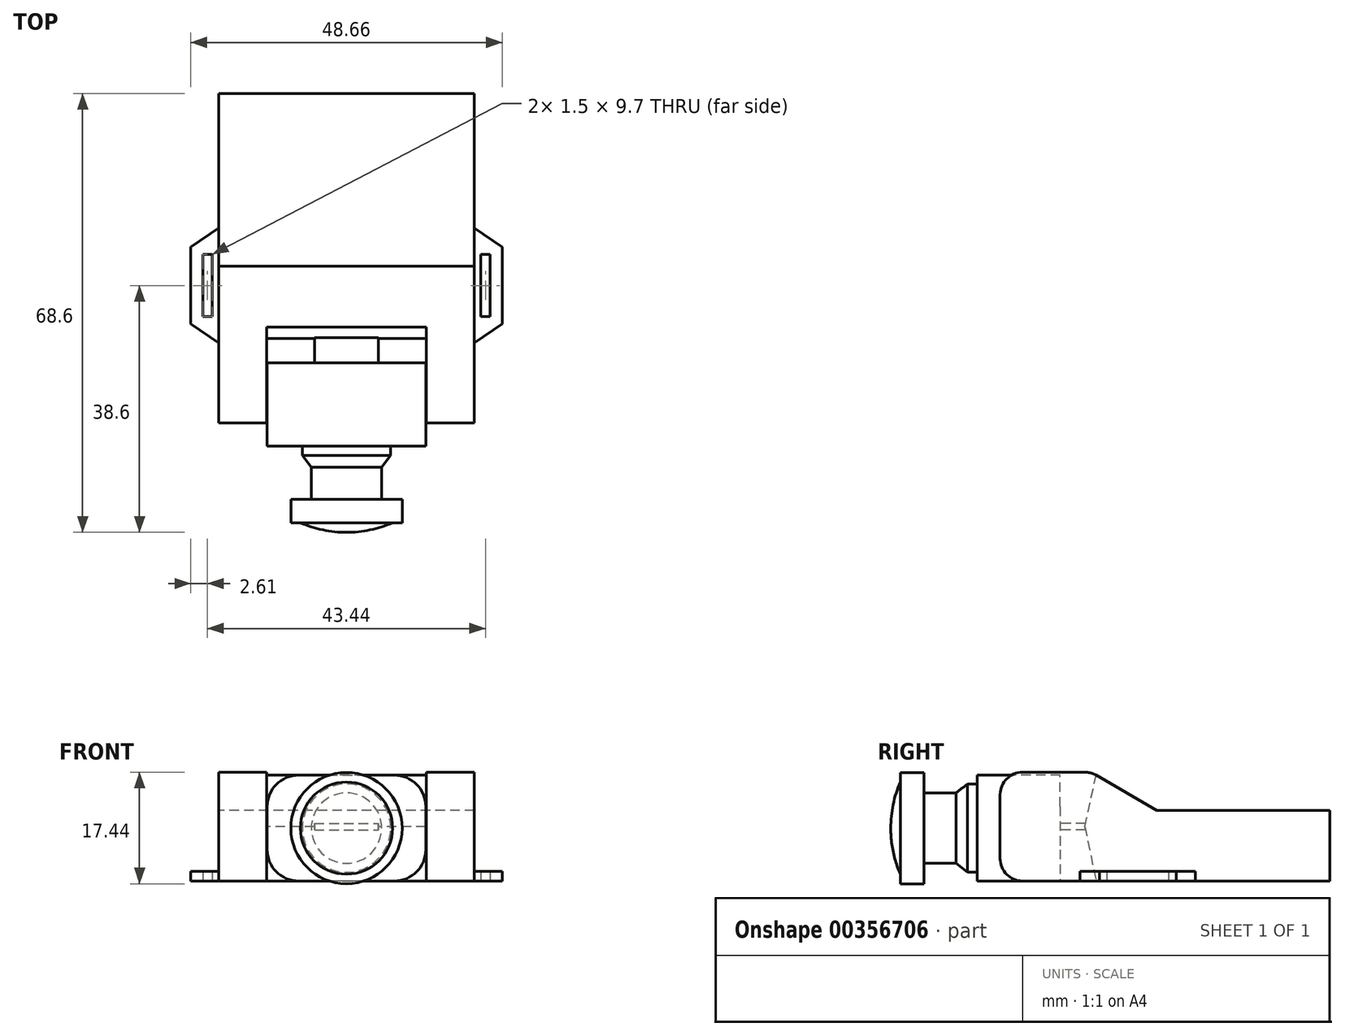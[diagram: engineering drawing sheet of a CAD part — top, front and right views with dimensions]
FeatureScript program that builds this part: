
annotation { "Feature Type Name" : "Feature", "Feature Type Description" : "" }
export const myFeature = defineFeature(function(context is Context, id is Id, definition is map)
    precondition{}
    {
        {
            var Q0;
            Q0=qCreatedBy(makeId("Right.planeOp"),FACE);
            var sketch = newSketch(context, id + "F0", { "sketchPlane" : qUnion([Q0])});
            skLineSegment(sketch, "E0.bottom", {"start": v(25.75, 11) * mm, "end": v(-1.25, 11) * mm});
            skLineSegment(sketch, "E0.top", {"start": v(25.75, 0) * mm, "end": v(-22.25, 0) * mm});
            skLineSegment(sketch, "E0.left", {"start": v(25.75, 11) * mm, "end": v(25.75, 0) * mm});
            skLineSegment(sketch, "E1", {"start": v(-25.75, 3.5) * mm, "end": v(-25.75, 13.5) * mm});
            skLineSegment(sketch, "E2", {"start": v(-22.25, 17) * mm, "end": v(-12.5, 17) * mm});
            skLineSegment(sketch, "E3", {"start": v(-10.75, 16.53) * mm, "end": v(-1.25, 11) * mm});
            skArc(sketch, "E4", {"start": v(-10.75, 16.53) * mm, "mid": v(-11.6, 16.88) * mm, "end": v(-12.5, 17) * mm});
            skArc(sketch, "E5", {"start": v(-25.75, 3.5) * mm, "mid": v(-24.72, 1.03) * mm, "end": v(-22.25, 0) * mm});
            skArc(sketch, "E6", {"start": v(-22.25, 17) * mm, "mid": v(-24.72, 15.97) * mm, "end": v(-25.75, 13.5) * mm});
            skSolve(sketch);
        }
        {
            var Q0;
            Q0=makeQuery(id+"F0.imprint","IMPRINT",FACE,{"disambiguationData":[TD([[makeQuery(id+"F0.imprint","IMPRINT",EDGE,{"derivedFrom":sQuery(id+"F0.wireOp",EDGE,"E0.bottom")}),1.0]])]});
            extrude(context, id + "F1", {"entities" : qUnion([Q0]), "endBound" : BoundingType.SYMMETRIC, "depth" : 40 * mm});
        }
        {
            var Q0;
            Q0=makeQuery(id+"F1.opExtrude","SWEPT_FACE",FACE,{"disambiguationData":[OSD([sQuery(id+"F0.wireOp",EDGE,"E2")])]});
            var sketch = newSketch(context, id + "F2", { "sketchPlane" : qUnion([Q0])});
            skLineSegment(sketch, "E7.bottom", {"start": v(-12.5, -12.5) * mm, "end": v(0, -12.5) * mm});
            skLineSegment(sketch, "E7.top", {"start": v(-12.5, -25.75) * mm, "end": v(0, -25.75) * mm});
            skLineSegment(sketch, "E7.left", {"start": v(-12.5, -12.5) * mm, "end": v(-12.5, -25.75) * mm});
            skLineSegment(sketch, "E7.right", {"start": v(12.5, -12.5) * mm, "end": v(12.5, -25.75) * mm});
            skLineSegment(sketch, "E8", {"start": v(0, -12.5) * mm, "end": v(12.5, -12.5) * mm});
            skLineSegment(sketch, "E9", {"start": v(0, -25.75) * mm, "end": v(12.5, -25.75) * mm});
            skLineSegment(sketch, "E10.0.1", {"start": v(-20, -25.75) * mm, "end": v(20, -25.75) * mm, "construction": true});
            skLineSegment(sketch, "E10.0.3", {"start": v(20, -25.75) * mm, "end": v(-20, -25.75) * mm});
            skLineSegment(sketch, "E11.0", {"start": v(20, -12.5) * mm, "end": v(-20, -12.5) * mm, "construction": true});
            skSolve(sketch);
        }
        {
            var Q0;
            Q0=qSketchRegion(id+"F2",true);
            var Q1;
            Q1=makeQuery(id+"F1.opExtrude","SWEPT_FACE",FACE,{"disambiguationData":[OSD([sQuery(id+"F0.wireOp",EDGE,"E0.top")])]});
            extrude(context, id + "F3", {"entities" : qUnion([Q0]), "operationType" : NewBodyOperationType.REMOVE, "endBound" : BoundingType.UP_TO_SURFACE, "oppositeDirection" : true, "endBoundEntityFace" : qUnion([Q1]), "depth" : 25 * mm});
        }
        {
            var Q0;
            Q0=makeQuery(id+"F3.boolean.opBoolean","COPY",FACE,{"derivedFrom":makeQuery(id+"F3.opExtrude","SWEPT_FACE",FACE,{"disambiguationData":[OSD([sQuery(id+"F2.wireOp",EDGE,"E7.left")])]})});
            var sketch = newSketch(context, id + "F4", { "sketchPlane" : qUnion([Q0])});
            skPoint(sketch, "E12.0", {"position": v(-10.75, 16.53) * mm});
            skPoint(sketch, "E12.1", {"position": v(-12.5, 17) * mm});
            skPoint(sketch, "E12.2", {"position": v(-12.5, 0) * mm});
            skLineSegment(sketch, "E13", {"start": v(-10.75, 16.53) * mm, "end": v(-12.5, 8.5) * mm});
            skLineSegment(sketch, "E14", {"start": v(-12.5, 8.5) * mm, "end": v(-10.75, 0) * mm});
            skLineSegment(sketch, "E15", {"start": v(-10.75, 0) * mm, "end": v(-12.5, 0) * mm});
            skLineSegment(sketch, "E16", {"start": v(-12.5, 0) * mm, "end": v(-12.5, 8.5) * mm});
            skLineSegment(sketch, "E17", {"start": v(-12.5, 8.5) * mm, "end": v(-12.5, 17) * mm});
            skPoint(sketch, "E18.0", {"position": v(-11.6, 16.88) * mm});
            skArc(sketch, "E19.converted", {"start": v(-12.5, 17) * mm, "mid": v(-11.6, 16.88) * mm, "end": v(-10.75, 16.53) * mm});
            skSolve(sketch);
        }
        {
            var Q0;
            Q0=qSketchRegion(id+"F4",true);
            var Q1;
            Q1=makeQuery(id+"F3.boolean.opBoolean","COPY",FACE,{"derivedFrom":makeQuery(id+"F3.opExtrude","SWEPT_FACE",FACE,{"disambiguationData":[OSD([sQuery(id+"F2.wireOp",EDGE,"E7.right")])]})});
            extrude(context, id + "F5", {"entities" : qUnion([Q0]), "operationType" : NewBodyOperationType.REMOVE, "endBound" : BoundingType.UP_TO_SURFACE, "endBoundEntityFace" : qUnion([Q1]), "depth" : 25 * mm});
        }
        {
            var Q0;
            Q0=makeQuery(id+"F1.opExtrude","SWEPT_FACE",FACE,{"disambiguationData":[OSD([sQuery(id+"F0.wireOp",EDGE,"E0.top")])]});
            var sketch = newSketch(context, id + "F6", { "sketchPlane" : qUnion([Q0])});
            skLineSegment(sketch, "E20.0", {"start": v(-20, -4.75) * mm, "end": v(-20, 13.25) * mm});
            skLineSegment(sketch, "E21", {"start": v(-20, 13.25) * mm, "end": v(-24.33, 10.25) * mm});
            skLineSegment(sketch, "E22", {"start": v(-24.33, 10.25) * mm, "end": v(-24.33, 4.25) * mm});
            skLineSegment(sketch, "E23", {"start": v(-24.33, -1.75) * mm, "end": v(-20, -4.75) * mm});
            skLineSegment(sketch, "E24.bottom", {"start": v(-22.47, 9.1) * mm, "end": v(-20.97, 9.1) * mm});
            skLineSegment(sketch, "E24.top", {"start": v(-22.47, -0.6) * mm, "end": v(-20.97, -0.6) * mm});
            skLineSegment(sketch, "E24.left", {"start": v(-22.47, 9.1) * mm, "end": v(-22.47, 4.25) * mm});
            skLineSegment(sketch, "E24.right", {"start": v(-20.97, 9.1) * mm, "end": v(-20.97, 4.25) * mm});
            skLineSegment(sketch, "E25", {"start": v(-24.33, 4.25) * mm, "end": v(-24.33, -1.75) * mm});
            skLineSegment(sketch, "E26", {"start": v(-22.47, 4.25) * mm, "end": v(-22.47, -0.6) * mm});
            skLineSegment(sketch, "E27", {"start": v(-20.97, 4.25) * mm, "end": v(-20.97, -0.6) * mm});
            skLineSegment(sketch, "E28", {"start": v(-24.33, 4.25) * mm, "end": v(-22.47, 4.25) * mm, "construction": true});
            skPoint(sketch, "E29.orphan", {"position": v(-20, 22.25) * mm});
            skPoint(sketch, "E30.orphan", {"position": v(-20, -25.75) * mm});
            skSolve(sketch);
        }
        {
            var Q0;
            Q0=qSketchRegion(id+"F6",true);
            extrude(context, id + "F7", {"entities" : qUnion([Q0]), "oppositeDirection" : true, "depth" : 1.5 * mm});
        }
        {
            var Q0;
            Q0=makeQuery(id+"F7.opExtrude","SWEPT_BODY",BODY,{"disambiguationData":[OSD([sQuery(id+"F6.wireOp",EDGE,"E20.0"),sQuery(id+"F6.wireOp",EDGE,"E21"),sQuery(id+"F6.wireOp",EDGE,"E22"),sQuery(id+"F6.wireOp",EDGE,"E23"),sQuery(id+"F6.wireOp",EDGE,"E24.bottom"),sQuery(id+"F6.wireOp",EDGE,"E24.top"),sQuery(id+"F6.wireOp",EDGE,"E24.left"),sQuery(id+"F6.wireOp",EDGE,"E24.right"),sQuery(id+"F6.wireOp",EDGE,"E25"),sQuery(id+"F6.wireOp",EDGE,"E26"),sQuery(id+"F6.wireOp",EDGE,"E27")])]});
            var Q1;
            Q1=qCreatedBy(makeId("Right.planeOp"),FACE);
            mirror(context, id + "F8", {"operationType" : NewBodyOperationType.ADD, "entities" : qUnion([Q0]), "mirrorPlane" : qUnion([Q1])});
        }
        {
            var Q0;
            {var subQ2=sQuery(id+"F0.wireOp",EDGE,"E1");Q0=makeQuery(id+"F3.boolean.opBoolean","SPLIT",FACE,{"disambiguationData":[TD([makeQuery(id+"F3.opExtrude","SWEPT_FACE",FACE,{"disambiguationData":[OSD([sQuery(id+"F2.wireOp",EDGE,"E7.right")])]})])],"derivedFrom":makeQuery(id+"F1.opExtrude","SWEPT_FACE",FACE,{"disambiguationData":[OSD([subQ2])]})});}
            cPlane(context, id + "F9", {"entities" : qUnion([Q0]), "cplaneType" : CPlaneType.OFFSET, "offset" : 3.6 * mm, "width" : 150 * mm, "height" : 150 * mm});
        }
        {
            var Q0;
            Q0=qCreatedBy(id+"F9.planeOp",FACE);
            var sketch = newSketch(context, id + "F10", { "sketchPlane" : qUnion([Q0])});
            skLineSegment(sketch, "E31.bottom", {"start": v(-12.4, 16.53) * mm, "end": v(0, 16.53) * mm});
            skLineSegment(sketch, "E31.top", {"start": v(-12.4, 0) * mm, "end": v(0, 0) * mm});
            skLineSegment(sketch, "E31.left", {"start": v(-12.4, 11.63) * mm, "end": v(-12.4, 4.9) * mm});
            skLineSegment(sketch, "E31.right", {"start": v(12.4, 11.63) * mm, "end": v(12.4, 4.9) * mm});
            skArc(sketch, "E32", {"start": v(-7.5, 16.53) * mm, "mid": v(-10.96, 15.1) * mm, "end": v(-12.4, 11.63) * mm});
            skArc(sketch, "E33", {"start": v(12.4, 11.63) * mm, "mid": v(10.96, 15.1) * mm, "end": v(7.5, 16.53) * mm});
            skArc(sketch, "E34", {"start": v(7.5, 0) * mm, "mid": v(10.96, 1.44) * mm, "end": v(12.4, 4.9) * mm});
            skArc(sketch, "E35", {"start": v(-12.4, 4.9) * mm, "mid": v(-10.96, 1.44) * mm, "end": v(-7.5, 0) * mm});
            skLineSegment(sketch, "E36.0", {"start": v(12.5, 16.53) * mm, "end": v(12.4, 16.53) * mm, "construction": true});
            skLineSegment(sketch, "E36.1", {"start": v(12.5, 0) * mm, "end": v(12.4, 0) * mm, "construction": true});
            skLineSegment(sketch, "E37", {"start": v(0, 16.53) * mm, "end": v(-7.5, 16.53) * mm, "construction": true});
            skLineSegment(sketch, "E38", {"start": v(0, 0) * mm, "end": v(-7.5, 0) * mm, "construction": true});
            skLineSegment(sketch, "E39", {"start": v(0, 16.53) * mm, "end": v(12.4, 16.53) * mm});
            skLineSegment(sketch, "E40", {"start": v(0, 0) * mm, "end": v(12.4, 0) * mm});
            skLineSegment(sketch, "E41.trimOffspring", {"start": v(-12.4, 16.53) * mm, "end": v(-12.5, 16.53) * mm, "construction": true});
            skLineSegment(sketch, "E42.trimOffspring", {"start": v(7.5, 16.53) * mm, "end": v(0, 16.53) * mm, "construction": true});
            skLineSegment(sketch, "E43.trimOffspring", {"start": v(7.5, 0) * mm, "end": v(0, 0) * mm, "construction": true});
            skLineSegment(sketch, "E44.trimOffspring", {"start": v(-12.4, 0) * mm, "end": v(-12.5, 0) * mm, "construction": true});
            skSolve(sketch);
        }
        {
            var Q0;
            Q0=qSketchRegion(id+"F10",true);
            extrude(context, id + "F11", {"entities" : qUnion([Q0]), "oppositeDirection" : true, "depth" : 13 * mm});
        }
        {
            var Q0;
            Q0=makeQuery(id+"F11.opExtrude","CAP_FACE",FACE,{"disambiguationData":[OSD([sQuery(id+"F10.wireOp",EDGE,"E31.bottom"),sQuery(id+"F10.wireOp",EDGE,"E31.top"),sQuery(id+"F10.wireOp",EDGE,"E31.left"),sQuery(id+"F10.wireOp",EDGE,"E31.right"),sQuery(id+"F10.wireOp",EDGE,"E32"),sQuery(id+"F10.wireOp",EDGE,"E33"),sQuery(id+"F10.wireOp",EDGE,"E34"),sQuery(id+"F10.wireOp",EDGE,"E35"),sQuery(id+"F10.wireOp",EDGE,"E39"),sQuery(id+"F10.wireOp",EDGE,"E40")])],"isStart":false});
            var sketch = newSketch(context, id + "F12", { "sketchPlane" : qUnion([Q0])});
            skLineSegment(sketch, "E45.0", {"start": v(-12.5, 8.5) * mm, "end": v(12.5, 8.5) * mm, "construction": true});
            skPoint(sketch, "E46.0", {"position": v(0, 16.53) * mm});
            skPoint(sketch, "E46.1", {"position": v(0, 0) * mm});
            skLineSegment(sketch, "E47.bottom", {"start": v(-5, 9) * mm, "end": v(0, 9) * mm});
            skLineSegment(sketch, "E47.top", {"start": v(-5, 8) * mm, "end": v(0, 8) * mm});
            skLineSegment(sketch, "E47.left", {"start": v(-5, 9) * mm, "end": v(-5, 8.5) * mm});
            skLineSegment(sketch, "E47.right", {"start": v(5, 9) * mm, "end": v(5, 8.5) * mm});
            skLineSegment(sketch, "E48", {"start": v(0, 9) * mm, "end": v(5, 9) * mm});
            skLineSegment(sketch, "E49", {"start": v(0, 8) * mm, "end": v(5, 8) * mm});
            skLineSegment(sketch, "E50", {"start": v(-5, 8.5) * mm, "end": v(-5, 8) * mm});
            skLineSegment(sketch, "E51", {"start": v(5, 8.5) * mm, "end": v(5, 8) * mm});
            skLineSegment(sketch, "E52", {"start": v(0, 16.53) * mm, "end": v(0, 0) * mm, "construction": true});
            skSolve(sketch);
        }
        {
            var Q0;
            Q0=qSketchRegion(id+"F12",true);
            var Q1;
            Q1=makeQuery(id+"F1.opExtrude","SWEPT_FACE",FACE,{"disambiguationData":[OSD([sQuery(id+"F0.wireOp",EDGE,"E0.left")])]});
            extrude(context, id + "F13", {"entities" : qUnion([Q0]), "operationType" : NewBodyOperationType.ADD, "endBound" : BoundingType.UP_TO_SURFACE, "endBoundEntityFace" : qUnion([Q1]), "depth" : 25 * mm});
        }
        {
            var Q0;
            Q0=qCreatedBy(makeId("Right.planeOp"),FACE);
            var sketch = newSketch(context, id + "F14", { "sketchPlane" : qUnion([Q0])});
            skLineSegment(sketch, "E53.0.0", {"start": v(-29.35, 11.63) * mm, "end": v(-29.35, 4.9) * mm});
            skLineSegment(sketch, "E53.0.1", {"start": v(-29.35, 4.9) * mm, "end": v(-29.35, 0) * mm});
            skLineSegment(sketch, "E53.0.3", {"start": v(-29.35, 0) * mm, "end": v(-29.35, 4.9) * mm, "construction": true});
            skLineSegment(sketch, "E53.0.4", {"start": v(-29.35, 4.9) * mm, "end": v(-29.35, 11.63) * mm, "construction": true});
            skLineSegment(sketch, "E53.0.5", {"start": v(-29.35, 11.63) * mm, "end": v(-29.35, 16.53) * mm});
            skLineSegment(sketch, "E53.0.7", {"start": v(-29.35, 16.53) * mm, "end": v(-29.35, 11.63) * mm, "construction": true});
            skLineSegment(sketch, "E54", {"start": v(-29.35, 8.26) * mm, "end": v(-41.35, 8.26) * mm});
            skPoint(sketch, "E54.endSnap0", {"position": v(-29.35, 8.26) * mm});
            skLineSegment(sketch, "E55", {"start": v(-41.35, 8.26) * mm, "end": v(-41.35, 1.06) * mm, "construction": true});
            skLineSegment(sketch, "E56", {"start": v(-41.35, 1.06) * mm, "end": v(-41.35, -0.44) * mm});
            skLineSegment(sketch, "E57", {"start": v(-41.35, -0.44) * mm, "end": v(-37.65, -0.44) * mm});
            skLineSegment(sketch, "E58", {"start": v(-37.65, -0.44) * mm, "end": v(-37.65, 2.76) * mm});
            skLineSegment(sketch, "E59", {"start": v(-37.65, 2.76) * mm, "end": v(-32.65, 2.76) * mm});
            skLineSegment(sketch, "E60", {"start": v(-32.65, 2.76) * mm, "end": v(-30.85, 1.36) * mm});
            skLineSegment(sketch, "E61", {"start": v(-30.85, 1.36) * mm, "end": v(-29.35, 1.36) * mm});
            skLineSegment(sketch, "E62", {"start": v(-29.35, 1.36) * mm, "end": v(-29.35, 8.26) * mm});
            skArc(sketch, "E63", {"start": v(-42.85, 8.26) * mm, "mid": v(-42.47, 4.59) * mm, "end": v(-41.35, 1.06) * mm});
            skLineSegment(sketch, "E64", {"start": v(-41.35, 8.26) * mm, "end": v(-42.85, 8.26) * mm});
            skSolve(sketch);
        }
        {
            var Q0;
            Q0=makeQuery(id+"F14.imprint","IMPRINT",FACE,{"disambiguationData":[TD([[makeQuery(id+"F14.imprint","IMPRINT",EDGE,{"derivedFrom":sQuery(id+"F14.wireOp",EDGE,"E54")}),1.0]])]});
            var Q1;
            Q1=sQuery(id+"F14.wireOp",EDGE,"E54");
            revolve(context, id + "F15", {"operationType" : NewBodyOperationType.ADD, "entities" : qUnion([Q0]), "axis" : qUnion([Q1]), "revolveType" : RevolveType.FULL});
        }
    });
